# Revit family: CAMPFIRE COMBO
name_source: partatom
category: Furniture Systems
units: mm (PartAtom-declared; Revit-internal decimal feet)

## family parameters
Always vertical = Yes
Cut with Voids When Loaded = No
Part Type = Normal
Room Calculation Point = No
Round Connector Dimension = Use Diameter
Shared = No
Work Plane-Based = No

## types (2) — shared parameters
30" Round Ottoman = F005-30X18
30" Round Ottoman Seat Fabric = <By Category>
30" Round Ottoman Side Fabric = <By Category>
Base = <By Category>
Configur-1_Log Ottoman-1_ Center Fabric = <By Category>
Configur-1_Log Ottoman-1_ Ends Fabric = <By Category>
Configur-1_Log Ottoman-2_ Center Fabric = <By Category>
Configur-1_Log Ottoman-2_ Ends Fabric = <By Category>
Configur-1_Log Ottoman-3_ Center Fabric = <By Category>
Configur-1_Log Ottoman-3_ Ends Fabric = <By Category>
Configur-1_Log Ottoman-4_ Center Fabric = <By Category>
Configur-1_Log Ottoman-4_ Ends Fabric = <By Category>
Configur-1_Log Ottoman-5_ Center Fabric = <By Category>
Configur-1_Log Ottoman-5_ Ends Fabric = <By Category>
Configur-1_Log Ottoman-6_ Center Fabric = <By Category>
Configur-1_Log Ottoman-6_ Ends Fabric = <By Category>
Configur-2_Log Ottoman-1_ Center Fabric = <By Category>
Configur-2_Log Ottoman-1_ Ends Fabric = <By Category>
Configur-2_Log Ottoman-2_ Center Fabric = <By Category>
Configur-2_Log Ottoman-2_ Ends Fabric = <By Category>
Configur-2_Log Ottoman-3_ Center Fabric = <By Category>
Configur-2_Log Ottoman-3_ Ends Fabric = <By Category>
Configur-2_Log Ottoman-4_ Center Fabric = <By Category>
Configur-2_Log Ottoman-4_ Ends Fabric = <By Category>
Description = Combo Products - CAMPFIRE COMBO
Glide = <By Category>
Manufacturer = FOMCORE
Model = CAMPFIRE COMBO
Triangle Flame = FK032-12X12X3
Triangle Frames-1 = <By Category>
Triangle Frames-2 = <By Category>
Triangle Frames-3 = <By Category>
URL = https://fomcore.com

## per-type parameters (varying)
| type | Configur-1 | Configur-1_Log Ottoman | Configur-2 | Configur-2_Log Ottoman |
| CAMPFIRE CONFIGUR-1 | Yes | FK501-18X15X16 | No | - |
| CAMPFIRE CONFIGUR-2 | No | - | Yes | FK501-18X15X48 |

## geometry (parser evidence)
native form markers: Sweep x2
no freeform markers — native parametric forms only
